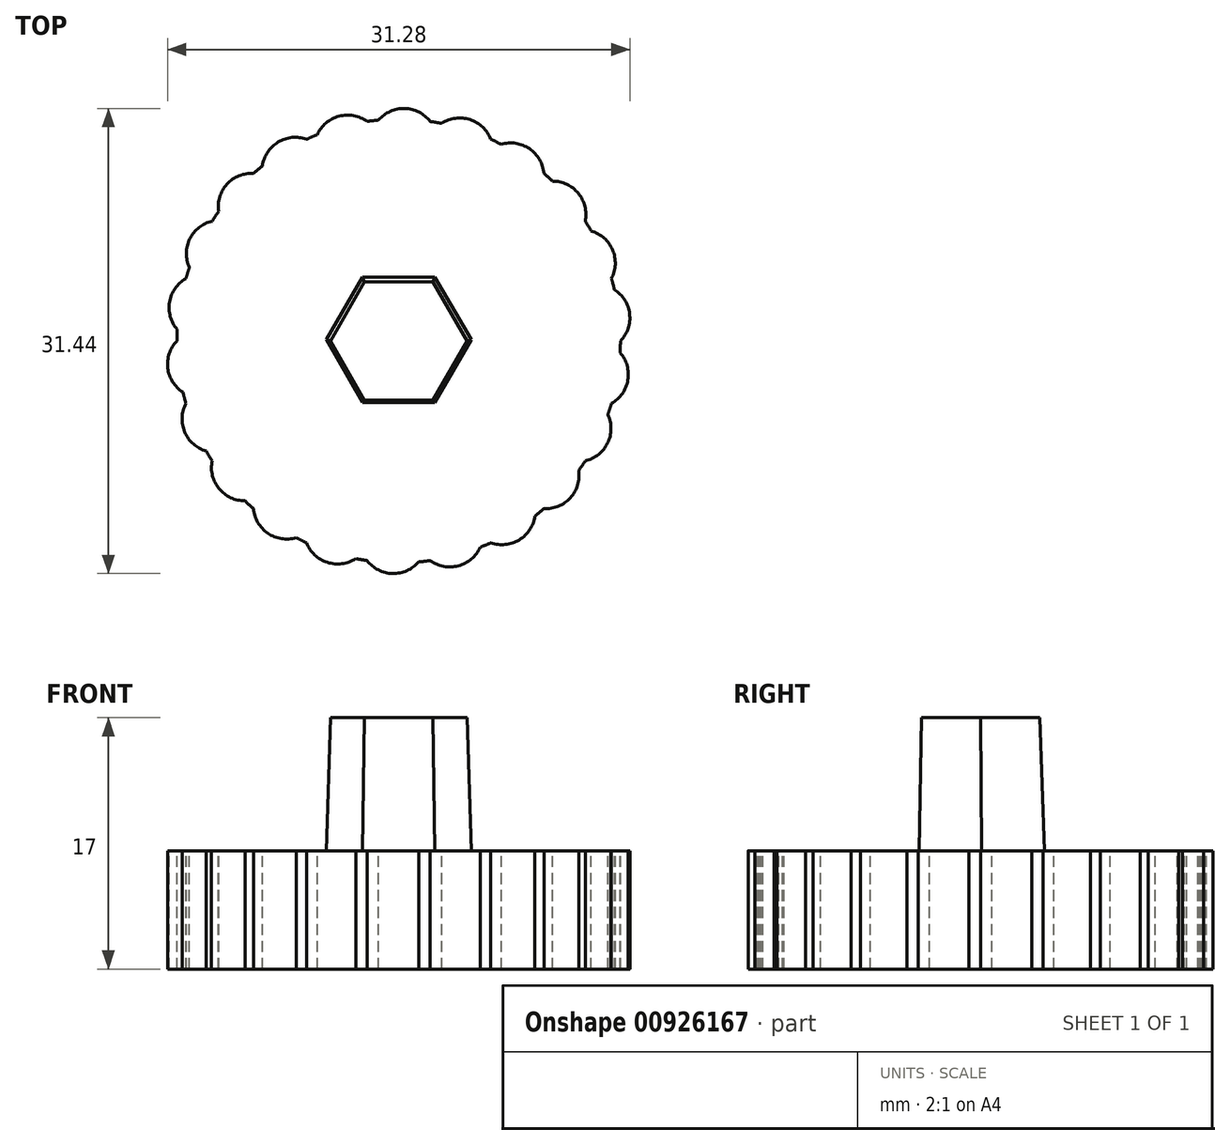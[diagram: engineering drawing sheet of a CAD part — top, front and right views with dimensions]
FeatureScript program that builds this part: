
annotation { "Feature Type Name" : "Feature", "Feature Type Description" : "" }
export const myFeature = defineFeature(function(context is Context, id is Id, definition is map)
    precondition{}
    {
        {
            var Q0;
            Q0=qCreatedBy(makeId("Top.planeOp"),FACE);
            var sketch = newSketch(context, id + "F0", { "sketchPlane" : qUnion([Q0])});
            skCircle(sketch, "E0.cCircle", {"center": v(0, 0) * mm, "radius": 4 * mm, "construction": true});
            skLineSegment(sketch, "E0.0", {"start": v(-2.3, -4) * mm, "end": v(-4.62, 0) * mm});
            skLineSegment(sketch, "E0.1", {"start": v(-4.62, 0) * mm, "end": v(-2.3, 4) * mm});
            skLineSegment(sketch, "E0.2", {"start": v(-2.3, 4) * mm, "end": v(2.3, 4) * mm});
            skLineSegment(sketch, "E0.3", {"start": v(2.3, 4) * mm, "end": v(4.62, 0) * mm});
            skLineSegment(sketch, "E0.4", {"start": v(4.62, 0) * mm, "end": v(2.3, -4) * mm});
            skLineSegment(sketch, "E0.5", {"start": v(2.3, -4) * mm, "end": v(-2.3, -4) * mm});
            skPoint(sketch, "E0.0.midPoint", {"position": v(-3.46, -2) * mm});
            skSolve(sketch);
        }
        {
            var Q0;
            Q0=qCreatedBy(makeId("Top.planeOp"),FACE);
            cPlane(context, id + "F1", {"entities" : qUnion([Q0]), "cplaneType" : CPlaneType.OFFSET, "offset" : 9 * mm, "oppositeDirection" : true, "width" : 150 * mm, "height" : 150 * mm});
        }
        {
            var Q0;
            Q0=qCreatedBy(id+"F1.planeOp",FACE);
            var sketch = newSketch(context, id + "F2", { "sketchPlane" : qUnion([Q0])});
            skCircle(sketch, "E1.cCircle", {"center": v(0, 0.08) * mm, "radius": 4.25 * mm, "construction": true});
            skLineSegment(sketch, "E1.0", {"start": v(-4.9, 0.08) * mm, "end": v(-2.45, 4.33) * mm});
            skLineSegment(sketch, "E1.1", {"start": v(-2.45, 4.33) * mm, "end": v(2.45, 4.33) * mm});
            skLineSegment(sketch, "E1.2", {"start": v(2.45, 4.33) * mm, "end": v(4.9, 0.08) * mm});
            skLineSegment(sketch, "E1.3", {"start": v(4.9, 0.08) * mm, "end": v(2.45, -4.17) * mm});
            skLineSegment(sketch, "E1.4", {"start": v(2.45, -4.17) * mm, "end": v(-2.45, -4.17) * mm});
            skLineSegment(sketch, "E1.5", {"start": v(-2.45, -4.17) * mm, "end": v(-4.9, 0.08) * mm});
            skPoint(sketch, "E1.0.midPoint", {"position": v(-3.68, 2.2) * mm});
            skCircle(sketch, "E2", {"center": v(0, 0) * mm, "radius": 15 * mm});
            skArc(sketch, "E3", {"start": v(15, 0) * mm, "mid": v(15.62, 1.83) * mm, "end": v(14.6, 3.47) * mm});
            skSolve(sketch);
        }
        {
            var Q0;
            Q0=makeQuery(id+"F2.imprint","IMPRINT",FACE,{"disambiguationData":[TD([[makeQuery(id+"F2.imprint","IMPRINT",EDGE,{"derivedFrom":sQuery(id+"F2.wireOp",EDGE,"E1.0")}),1.0]])]});
            var Q1;
            Q1=makeQuery(id+"F2.imprint","IMPRINT",FACE,{"disambiguationData":[TD([[makeQuery(id+"F2.imprint","IMPRINT",EDGE,{"derivedFrom":sQuery(id+"F2.wireOp",EDGE,"E1.0")}),-1.0]])]});
            extrude(context, id + "F3", {"entities" : qUnion([Q0, Q1]), "oppositeDirection" : true, "depth" : 8 * mm, "offsetDistance" : 25 * mm});
        }
        {
            var Q0;
            {var subQ0=sQuery(id+"F2.wireOp",EDGE,"E3");Q0=makeQuery(id+"F2.imprint","IMPRINT",FACE,{"disambiguationData":[TD([[makeQuery(id+"F2.imprint","IMPRINT",EDGE,{"derivedFrom":subQ0}),1.0]])]});}
            var Q1;
            Q1=makeQuery(id+"F3.opExtrude","CAP_FACE",FACE,{"disambiguationData":[OSD([sQuery(id+"F2.wireOp",EDGE,"E1.0"),sQuery(id+"F2.wireOp",EDGE,"E1.1"),sQuery(id+"F2.wireOp",EDGE,"E1.2"),sQuery(id+"F2.wireOp",EDGE,"E1.3"),sQuery(id+"F2.wireOp",EDGE,"E1.4"),sQuery(id+"F2.wireOp",EDGE,"E1.5"),sQuery(id+"F2.wireOp",EDGE,"E2")])],"isStart":false});
            extrude(context, id + "F4", {"entities" : qUnion([Q0]), "endBound" : BoundingType.UP_TO_SURFACE, "oppositeDirection" : true, "depth" : 25 * mm, "endBoundEntityFace" : qUnion([Q1]), "offsetDistance" : 25 * mm});
        }
        {
            var Q0;
            Q0=makeQuery(id+"F4.opExtrude","SWEPT_BODY",BODY,{"disambiguationData":[OSD([sQuery(id+"F2.wireOp",EDGE,"E2"),sQuery(id+"F2.wireOp",EDGE,"E3")])]});
            var Q1;
            Q1=makeQuery(id+"F3.opExtrude","CAP_EDGE",EDGE,{"disambiguationData":[OSD([sQuery(id+"F2.wireOp",EDGE,"E2")])],"isStart":true});
            circularPattern(context, id + "F5", {"operationType" : NewBodyOperationType.ADD, "entities" : qUnion([Q0]), "axis" : qUnion([Q1]), "angle" : 360 * degree, "instanceCount" : 22, "equalSpace" : true});
        }
        {
            var Q1;
            Q1=makeQuery(id+"F0.imprint","IMPRINT",FACE,{"disambiguationData":[TD([[makeQuery(id+"F0.imprint","IMPRINT",EDGE,{"derivedFrom":sQuery(id+"F0.wireOp",EDGE,"E0.0")}),-1.0]])]});
            var Q2;
            Q2=makeQuery(id+"F2.imprint","IMPRINT",FACE,{"disambiguationData":[TD([[makeQuery(id+"F2.imprint","IMPRINT",EDGE,{"derivedFrom":sQuery(id+"F2.wireOp",EDGE,"E1.0")}),-1.0]])]});
            loft(context, id + "F6", {"operationType" : NewBodyOperationType.ADD, "sheetProfilesArray" : [{ "sheetProfileEntities" : qUnion([Q1]) }, { "sheetProfileEntities" : qUnion([Q2]) }]});
        }
    });
